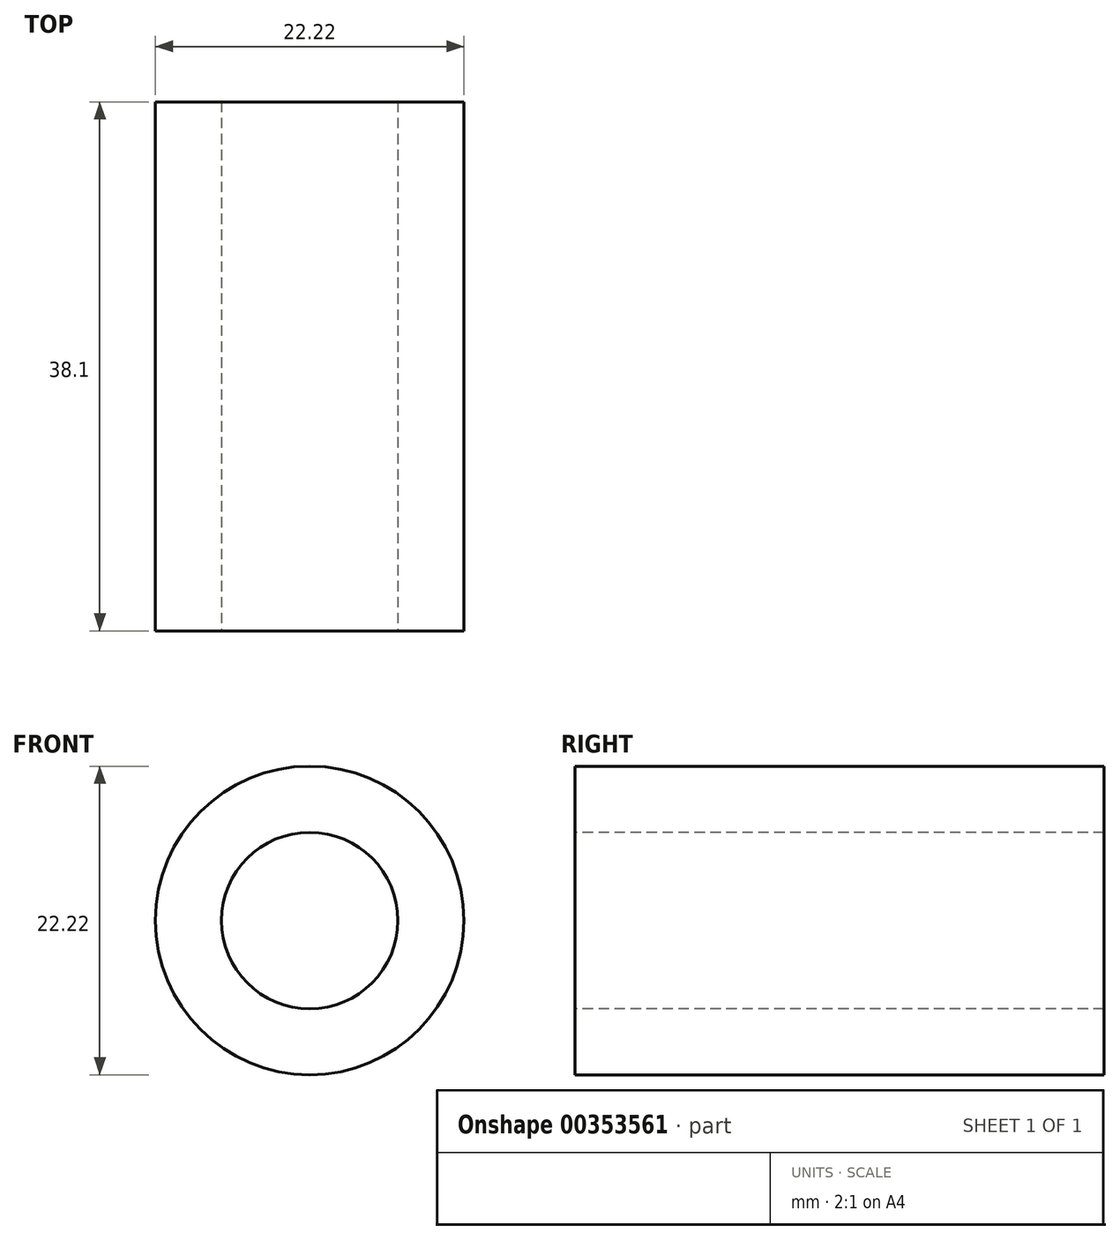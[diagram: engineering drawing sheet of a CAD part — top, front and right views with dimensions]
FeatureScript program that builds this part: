
annotation { "Feature Type Name" : "Feature", "Feature Type Description" : "" }
export const myFeature = defineFeature(function(context is Context, id is Id, definition is map)
    precondition{}
    {
        {
            var Q0;
            Q0=qCreatedBy(makeId("Front.planeOp"),FACE);
            var sketch = newSketch(context, id + "F0", { "sketchPlane" : qUnion([Q0])});
            skCircle(sketch, "E0", {"center": v(0, 0) * mm, "radius": 11.11 * mm});
            skSolve(sketch);
        }
        {
            var Q0;
            Q0 = qSketchRegion(id + "F0", true);
            extrude(context, id + "F1", {"entities" : qUnion([Q0]), "depth" : 38.1 * mm, "symmetric" : true});
        }
        {
            var Q0;
            Q0=makeQuery(id+"F1.opExtrude","CAP_FACE",FACE,{"disambiguationData":[OSD([sQuery(id+"F0.wireOp",EDGE,"E0")])],"isStart":false});
            var sketch = newSketch(context, id + "F2", { "sketchPlane" : qUnion([Q0])});
            skCircle(sketch, "E1", {"center": v(0, 0) * mm, "radius": 6.35 * mm});
            skSolve(sketch);
        }
        {
            var Q0;
            Q0=makeQuery(id+"F2.imprint","IMPRINT",FACE,{"disambiguationData":[TD([[makeQuery(id+"F2.imprint","IMPRINT",EDGE,{"derivedFrom":sQuery(id+"F2.wireOp",EDGE,"E1")}),1.0]])]});
            extrude(context, id + "F3", {"entities" : qUnion([Q0]), "operationType" : NewBodyOperationType.REMOVE, "endBound" : BoundingType.THROUGH_ALL, "oppositeDirection" : true, "depth" : 25.4 * mm});
        }
    });
